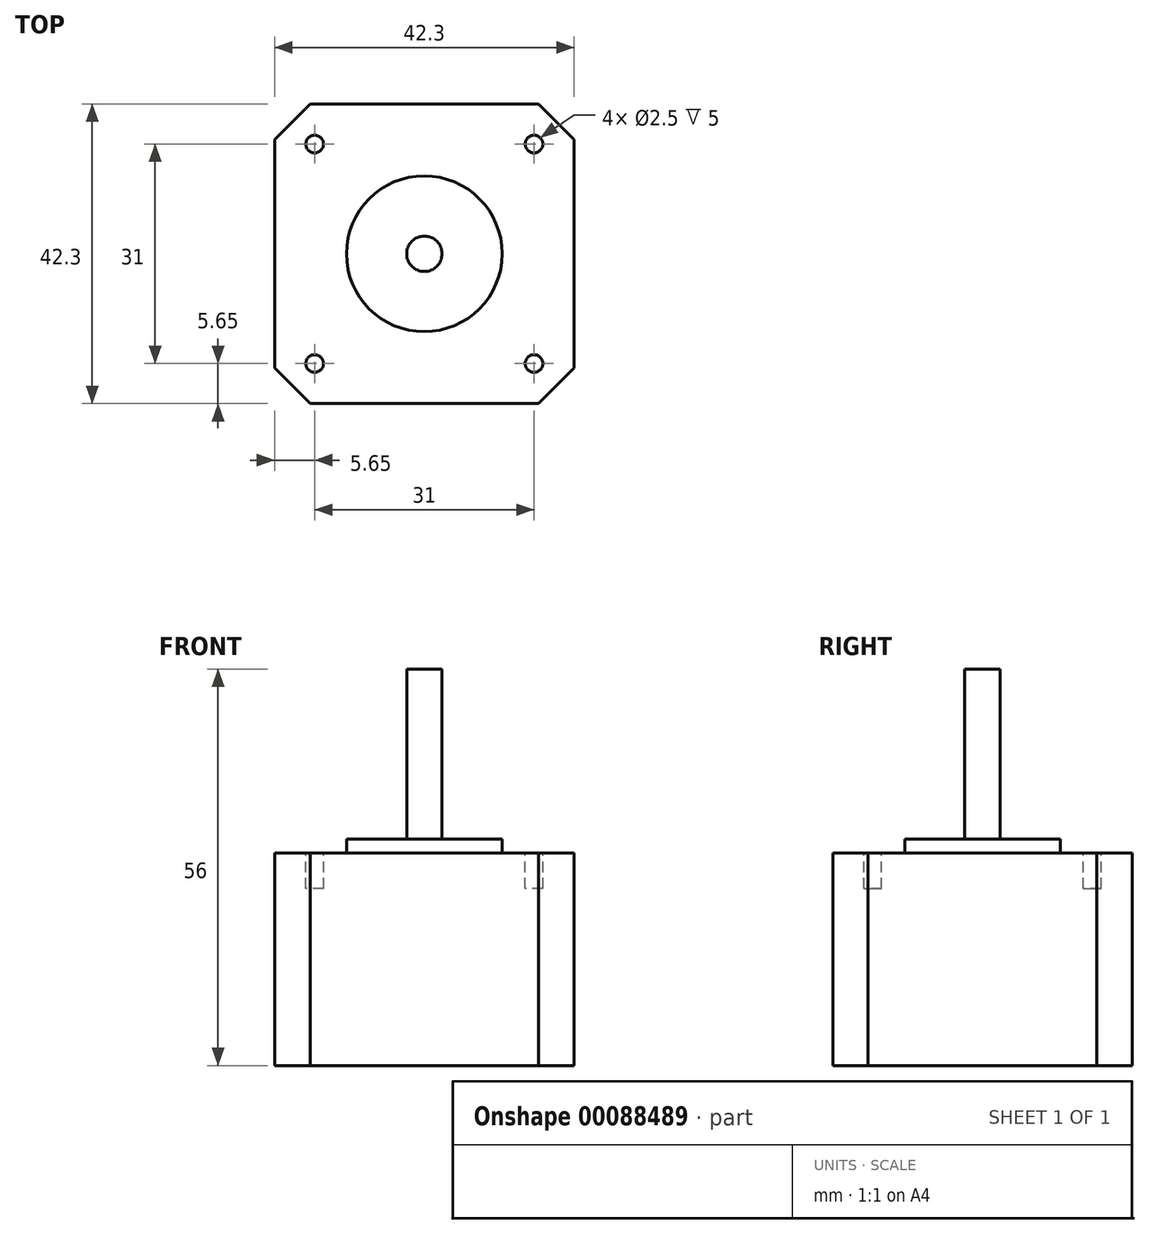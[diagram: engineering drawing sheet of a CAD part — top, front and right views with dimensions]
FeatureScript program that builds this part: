
annotation { "Feature Type Name" : "Feature", "Feature Type Description" : "" }
export const myFeature = defineFeature(function(context is Context, id is Id, definition is map)
    precondition{}
    {
        {
            var Q0;
            Q0=qCreatedBy(makeId("Top.planeOp"),FACE);
            var sketch = newSketch(context, id + "F0", { "sketchPlane" : qUnion([Q0])});
            skLineSegment(sketch, "E0.bottom", {"start": v(-21.15, 21.15) * mm, "end": v(21.15, 21.15) * mm});
            skLineSegment(sketch, "E0.top", {"start": v(-21.15, -21.15) * mm, "end": v(21.15, -21.15) * mm});
            skLineSegment(sketch, "E0.left", {"start": v(-21.15, 21.15) * mm, "end": v(-21.15, -21.15) * mm});
            skLineSegment(sketch, "E0.right", {"start": v(21.15, 21.15) * mm, "end": v(21.15, -21.15) * mm});
            skLineSegment(sketch, "E1", {"start": v(-21.15, -21.15) * mm, "end": v(21.15, 21.15) * mm, "construction": true});
            skCircle(sketch, "E2", {"center": v(0, 0) * mm, "radius": 10 * mm, "construction": true});
            skSolve(sketch);
        }
        {
            var Q0;
            Q0=qSketchRegion(id+"F0",true);
            extrude(context, id + "F1", {"entities" : qUnion([Q0]), "depth" : 30 * mm});
        }
        {
            var Q0;
            Q0=makeQuery(id+"F1.opExtrude","SWEPT_EDGE",EDGE,{"disambiguationData":[OSD([sQuery(id+"F0.wireOp",EDGE,"E0.top"),sQuery(id+"F0.wireOp",EDGE,"E0.right")])]});
            var Q1;
            Q1=makeQuery(id+"F1.opExtrude","SWEPT_EDGE",EDGE,{"disambiguationData":[OSD([sQuery(id+"F0.wireOp",EDGE,"E0.top"),sQuery(id+"F0.wireOp",EDGE,"E0.left")])]});
            var Q2;
            Q2=makeQuery(id+"F1.opExtrude","SWEPT_EDGE",EDGE,{"disambiguationData":[OSD([sQuery(id+"F0.wireOp",EDGE,"E0.bottom"),sQuery(id+"F0.wireOp",EDGE,"E0.left")])]});
            var Q3;
            Q3=makeQuery(id+"F1.opExtrude","SWEPT_EDGE",EDGE,{"disambiguationData":[OSD([sQuery(id+"F0.wireOp",EDGE,"E0.bottom"),sQuery(id+"F0.wireOp",EDGE,"E0.right")])]});
            chamfer(context, id + "F2", {"entities" : qUnion([Q0, Q1, Q2, Q3]), "width" : 5 * mm, "tangentPropagation" : true});
        }
        {
            var Q0;
            Q0=qCreatedBy(makeId("Right.planeOp"),FACE);
            var sketch = newSketch(context, id + "F3", { "sketchPlane" : qUnion([Q0])});
            skLineSegment(sketch, "E3", {"start": v(0, 30) * mm, "end": v(0, 56) * mm});
            skLineSegment(sketch, "E4", {"start": v(0, 56) * mm, "end": v(-2.5, 56) * mm});
            skLineSegment(sketch, "E5", {"start": v(-2.5, 56) * mm, "end": v(-2.5, 32) * mm});
            skLineSegment(sketch, "E6", {"start": v(-2.5, 32) * mm, "end": v(-11, 32) * mm});
            skLineSegment(sketch, "E7", {"start": v(-11, 32) * mm, "end": v(-11, 30) * mm});
            skLineSegment(sketch, "E8", {"start": v(-11, 30) * mm, "end": v(0, 30) * mm});
            skSolve(sketch);
        }
        {
            var Q0;
            Q0=makeQuery(id+"F3.imprint","IMPRINT",FACE,{"disambiguationData":[TD([[makeQuery(id+"F3.imprint","IMPRINT",EDGE,{"derivedFrom":sQuery(id+"F3.wireOp",EDGE,"E3")}),1.0]])]});
            var Q1;
            Q1=sQuery(id+"F3.wireOp",EDGE,"E3");
            revolve(context, id + "F4", {"operationType" : NewBodyOperationType.ADD, "entities" : qUnion([Q0]), "axis" : qUnion([Q1]), "revolveType" : RevolveType.FULL});
        }
        {
            var Q0;
            Q0=makeQuery(id+"F1.opExtrude","CAP_FACE",FACE,{"disambiguationData":[OSD([sQuery(id+"F0.wireOp",EDGE,"E0.bottom"),sQuery(id+"F0.wireOp",EDGE,"E0.top"),sQuery(id+"F0.wireOp",EDGE,"E0.left"),sQuery(id+"F0.wireOp",EDGE,"E0.right")])],"isStart":false});
            var sketch = newSketch(context, id + "F5", { "sketchPlane" : qUnion([Q0])});
            skLineSegment(sketch, "E9.bottom", {"start": v(15.5, 15.5) * mm, "end": v(-15.5, 15.5) * mm, "construction": true});
            skLineSegment(sketch, "E9.top", {"start": v(15.5, -15.5) * mm, "end": v(-15.5, -15.5) * mm, "construction": true});
            skLineSegment(sketch, "E9.left", {"start": v(15.5, 15.5) * mm, "end": v(15.5, -15.5) * mm, "construction": true});
            skLineSegment(sketch, "E9.right", {"start": v(-15.5, 15.5) * mm, "end": v(-15.5, -15.5) * mm, "construction": true});
            skPoint(sketch, "E9.middle", {"position": v(0, 0) * mm});
            skCircle(sketch, "E10", {"center": v(-15.5, 15.5) * mm, "radius": 1.25 * mm});
            skCircle(sketch, "E11", {"center": v(15.5, 15.5) * mm, "radius": 1.25 * mm});
            skCircle(sketch, "E12", {"center": v(15.5, -15.5) * mm, "radius": 1.25 * mm});
            skCircle(sketch, "E13", {"center": v(-15.5, -15.5) * mm, "radius": 1.25 * mm});
            skSolve(sketch);
        }
        {
            var Q0;
            Q0=qSketchRegion(id+"F5",true);
            extrude(context, id + "F6", {"entities" : qUnion([Q0]), "operationType" : NewBodyOperationType.REMOVE, "oppositeDirection" : true, "depth" : 5 * mm});
        }
    });
